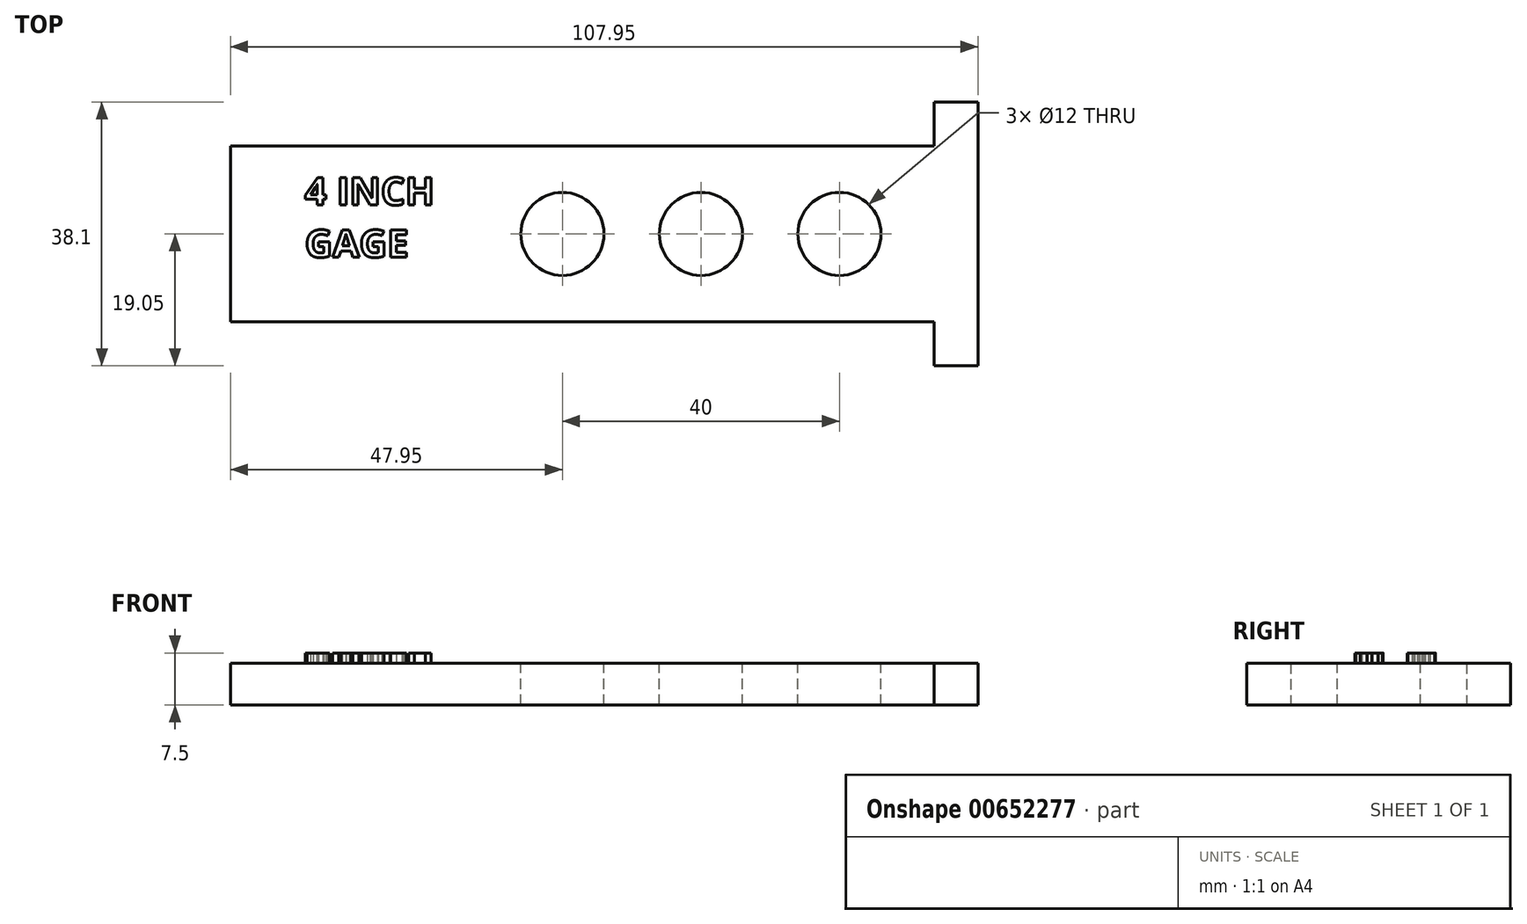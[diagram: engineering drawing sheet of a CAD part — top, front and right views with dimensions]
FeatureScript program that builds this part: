
annotation { "Feature Type Name" : "Feature", "Feature Type Description" : "" }
export const myFeature = defineFeature(function(context is Context, id is Id, definition is map)
    precondition{}
    {
        {
            var Q0;
            Q0=qCreatedBy(makeId("Top.planeOp"),FACE);
            var sketch = newSketch(context, id + "F0", { "sketchPlane" : qUnion([Q0])});
            skLineSegment(sketch, "E0.bottom", {"start": v(0, 0) * mm, "end": v(-101.6, 0) * mm});
            skLineSegment(sketch, "E0.top", {"start": v(0, 25.4) * mm, "end": v(-101.6, 25.4) * mm});
            skLineSegment(sketch, "E0.right", {"start": v(-101.6, 0) * mm, "end": v(-101.6, 25.4) * mm});
            skLineSegment(sketch, "E1.bottom", {"start": v(0, -6.35) * mm, "end": v(6.35, -6.35) * mm});
            skLineSegment(sketch, "E1.top", {"start": v(0, 31.75) * mm, "end": v(6.35, 31.75) * mm});
            skLineSegment(sketch, "E1.left", {"start": v(0, -6.35) * mm, "end": v(0, 0) * mm});
            skLineSegment(sketch, "E1.right", {"start": v(6.35, -6.35) * mm, "end": v(6.35, 31.75) * mm});
            skLineSegment(sketch, "E2", {"start": v(-108.34, 12.7) * mm, "end": v(13.64, 12.7) * mm, "construction": true});
            skPoint(sketch, "E2.startSnap0", {"position": v(-101.6, 12.7) * mm});
            skLineSegment(sketch, "E3.trimOffspring", {"start": v(0, 25.4) * mm, "end": v(0, 31.75) * mm});
            skSolve(sketch);
        }
        {
            var Q0;
            Q0 = qSketchRegion(id + "F0", true);
            extrude(context, id + "F1", {"entities" : qUnion([Q0]), "depth" : 6 * mm, "offsetDistance" : 25 * mm});
        }
        {
            var Q0;
            Q0=makeQuery(id+"F1.opExtrude","CAP_FACE",FACE,{"disambiguationData":[OSD([sQuery(id+"F0.wireOp",EDGE,"E0.bottom"),sQuery(id+"F0.wireOp",EDGE,"E0.top"),sQuery(id+"F0.wireOp",EDGE,"E0.right"),sQuery(id+"F0.wireOp",EDGE,"E1.bottom"),sQuery(id+"F0.wireOp",EDGE,"E1.top"),sQuery(id+"F0.wireOp",EDGE,"E1.left"),sQuery(id+"F0.wireOp",EDGE,"E1.right"),sQuery(id+"F0.wireOp",EDGE,"E3.trimOffspring")])],"isStart":false});
            var sketch = newSketch(context, id + "F2", { "sketchPlane" : qUnion([Q0])});
            skText(sketch, "E4", { "text": "4 INCH\nGAGE", "fontName": "OpenSans-Bold.ttf"});
            const initialGuessF2  = {"E4": [-0.09085, 0.01687, 1, 0, 0.004]};
            skSetInitialGuess(sketch, initialGuessF2);
            skSolve(sketch);
        }
        {
            var Q0;
            Q0 = qSketchRegion(id + "F2", true);
            extrude(context, id + "F3", {"entities" : qUnion([Q0]), "operationType" : NewBodyOperationType.ADD, "depth" : 1.5 * mm, "offsetDistance" : 25 * mm});
        }
        {
            var Q0;
            {var subQ0=sQuery(id+"F0.wireOp",EDGE,"E0.top");var subQ1=sQuery(id+"F0.wireOp",EDGE,"E1.bottom");var subQ2=sQuery(id+"F0.wireOp",EDGE,"E0.bottom");var subQ3=sQuery(id+"F0.wireOp",EDGE,"E1.top");var subQ4=sQuery(id+"F0.wireOp",EDGE,"E1.left");var subQ5=sQuery(id+"F0.wireOp",EDGE,"E1.right");var subQ6=sQuery(id+"F0.wireOp",EDGE,"E3.trimOffspring");var subQ7=sQuery(id+"F0.wireOp",EDGE,"E0.right");Q0=makeQuery(id+"F3.boolean.opBoolean","SPLIT",FACE,{"disambiguationData":[TD([makeQuery(id+"F1.opExtrude","SWEPT_FACE",FACE,{"disambiguationData":[OSD([subQ2])]})])],"derivedFrom":makeQuery(id+"F1.opExtrude","CAP_FACE",FACE,{"disambiguationData":[OSD([subQ2,subQ0,subQ7,subQ1,subQ3,subQ4,subQ5,subQ6])],"isStart":false})});}
            var sketch = newSketch(context, id + "F4", { "sketchPlane" : qUnion([Q0])});
            skLineSegment(sketch, "E5", {"start": v(-101.6, 12.7) * mm, "end": v(-5.7, 12.7) * mm, "construction": true});
            skPoint(sketch, "E6", {"position": v(-33.65, 12.7) * mm});
            skPoint(sketch, "E7", {"position": v(-13.65, 12.7) * mm});
            skPoint(sketch, "E8", {"position": v(-53.65, 12.7) * mm});
            skSolve(sketch);
        }
        {
            var Q0;
            Q0=sQuery(id+"F4.wireOp",VERTEX,"E8");
            var Q1;
            Q1=sQuery(id+"F4.wireOp",VERTEX,"E6");
            var Q2;
            Q2=sQuery(id+"F4.wireOp",VERTEX,"E7");
            var Q3;
            Q3=makeQuery(id+"F1.opExtrude","SWEPT_BODY",BODY,{"disambiguationData":[OSD([sQuery(id+"F0.wireOp",EDGE,"E0.bottom"),sQuery(id+"F0.wireOp",EDGE,"E0.top"),sQuery(id+"F0.wireOp",EDGE,"E0.right"),sQuery(id+"F0.wireOp",EDGE,"E1.bottom"),sQuery(id+"F0.wireOp",EDGE,"E1.top"),sQuery(id+"F0.wireOp",EDGE,"E1.left"),sQuery(id+"F0.wireOp",EDGE,"E1.right"),sQuery(id+"F0.wireOp",EDGE,"E3.trimOffspring")])]});
            hole(context, id + "F5", {"style" : HoleStyle.SIMPLE, "endStyle" : HoleEndStyle.THROUGH, "holeDiameter" : 12 * mm, "majorDiameter" : 5 * mm, "isTappedThrough" : true, "tappedDepth" : 12 * mm, "tapClearance" : 3, "locations" : qUnion([Q0, Q1, Q2]), "scope" : qUnion([Q3])});
        }
    });
